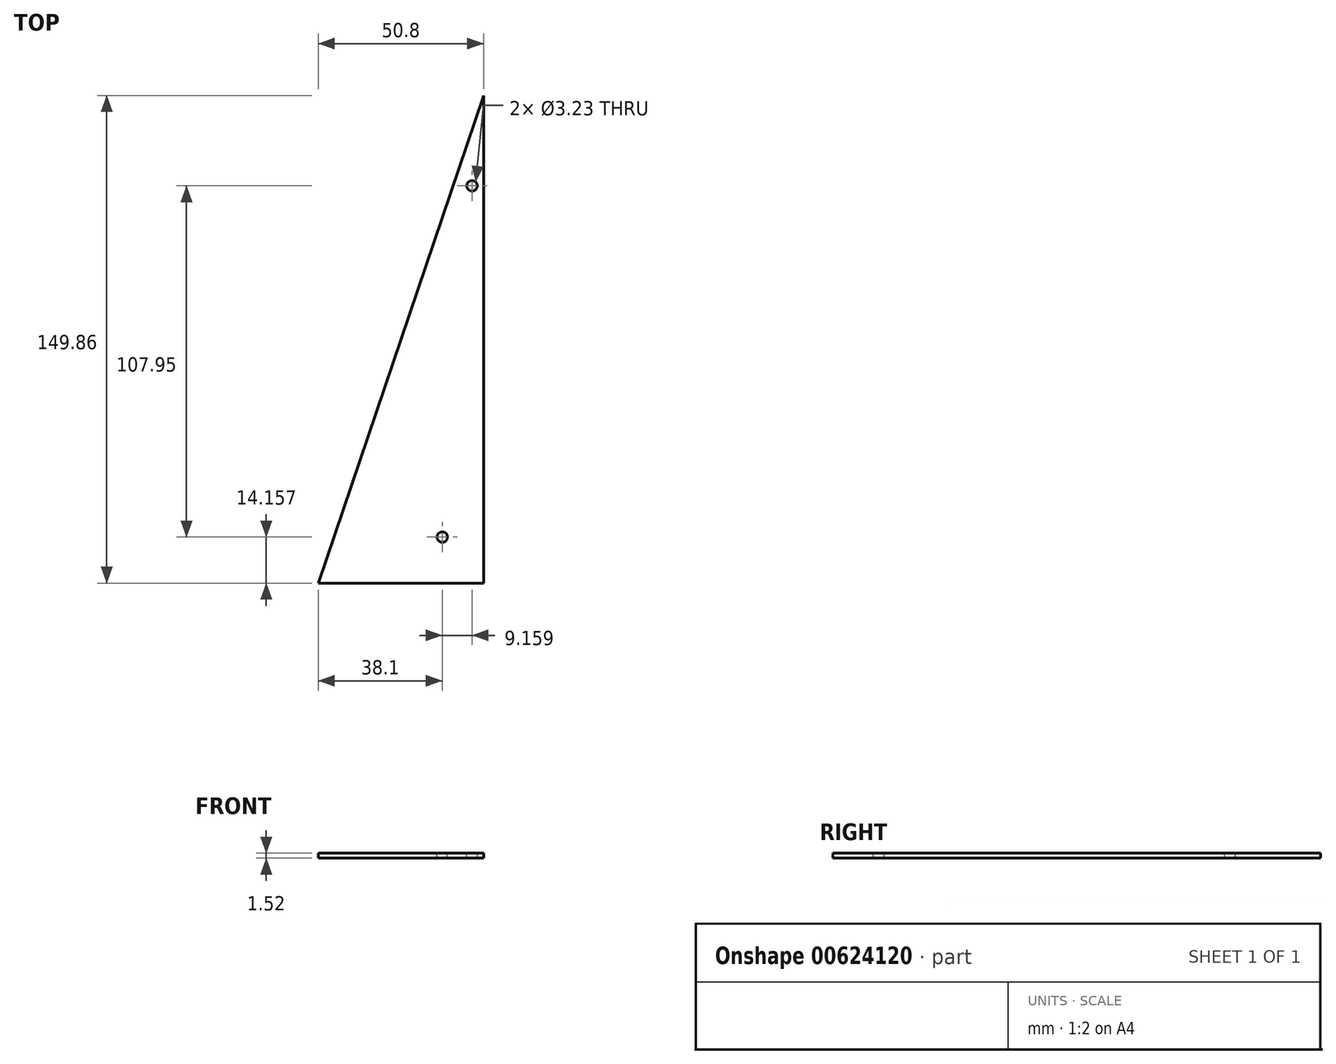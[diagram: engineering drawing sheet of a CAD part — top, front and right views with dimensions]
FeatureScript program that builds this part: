
annotation { "Feature Type Name" : "Feature", "Feature Type Description" : "" }
export const myFeature = defineFeature(function(context is Context, id is Id, definition is map)
    precondition{}
    {
        {
            var Q0;
            Q0=qCreatedBy(makeId("Top.planeOp"),FACE);
            var sketch = newSketch(context, id + "F0", { "sketchPlane" : qUnion([Q0])});
            skLineSegment(sketch, "E0.top", {"start": v(25.4, -74.93) * mm, "end": v(-25.4, -74.93) * mm});
            skLineSegment(sketch, "E0.left", {"start": v(25.4, 74.93) * mm, "end": v(25.4, -74.93) * mm});
            skPoint(sketch, "E0.middle", {"position": v(0, 0) * mm});
            skLineSegment(sketch, "E1", {"start": v(-25.4, -74.93) * mm, "end": v(25.4, 74.93) * mm});
            skPoint(sketch, "E0.bottom.end.orphan", {"position": v(-25.4, 74.93) * mm});
            skSolve(sketch);
        }
        {
            var Q0;
            Q0 = qSketchRegion(id + "F0", true);
            extrude(context, id + "F1", {"entities" : qUnion([Q0]), "depth" : 1.52 * mm, "offsetDistance" : 25.4 * mm});
        }
        {
            var Q0;
            Q0=makeQuery(id+"F1.opExtrude","CAP_FACE",FACE,{"disambiguationData":[OSD([sQuery(id+"F0.wireOp",EDGE,"E0.bottom"),sQuery(id+"F0.wireOp",EDGE,"E0.top"),sQuery(id+"F0.wireOp",EDGE,"E0.left"),sQuery(id+"F0.wireOp",EDGE,"E0.right")])],"isStart":false});
            var sketch = newSketch(context, id + "F2", { "sketchPlane" : qUnion([Q0])});
            skCircle(sketch, "E2", {"center": v(21.86, 47.18) * mm, "radius": 1.61 * mm});
            skCircle(sketch, "E3", {"center": v(12.7, -60.77) * mm, "radius": 1.61 * mm});
            skLineSegment(sketch, "E4", {"start": v(12.7, -60.77) * mm, "end": v(25.4, -60.77) * mm});
            skSolve(sketch);
        }
        {
            var Q0;
            Q0 = qSketchRegion(id + "F2", true);
            extrude(context, id + "F3", {"entities" : qUnion([Q0]), "operationType" : NewBodyOperationType.REMOVE, "oppositeDirection" : true, "depth" : 25.4 * mm, "offsetDistance" : 25.4 * mm});
        }
        {
            var Q0;
            Q0 = qSketchRegion(id + "F2", true);
            extrude(context, id + "F4", {"entities" : qUnion([Q0]), "operationType" : NewBodyOperationType.REMOVE, "depth" : 39.37 * mm, "offsetDistance" : 25.4 * mm});
        }
    });
